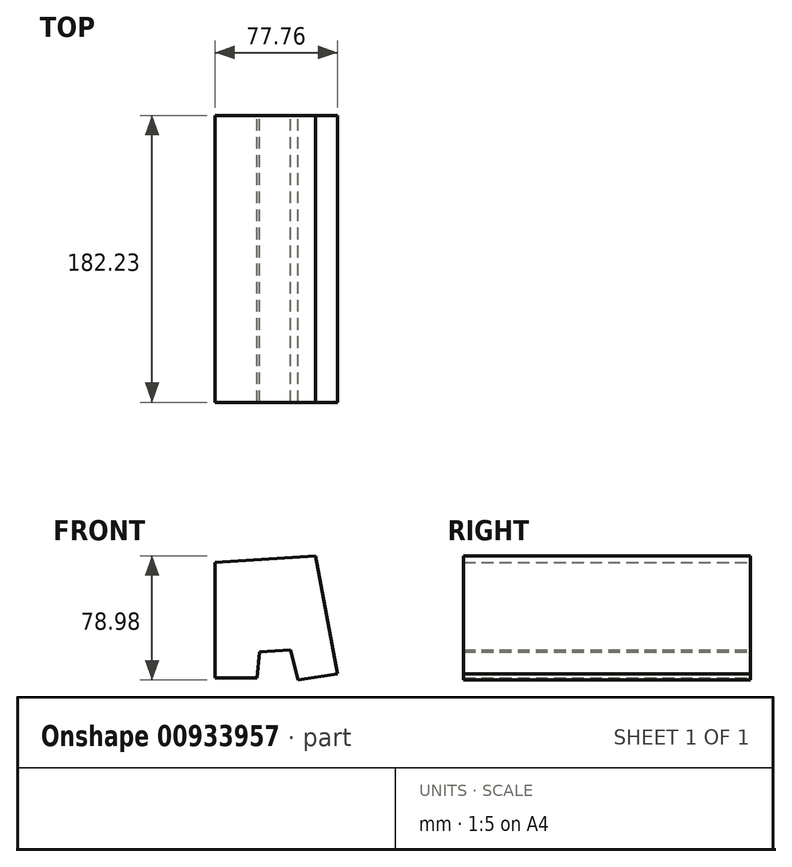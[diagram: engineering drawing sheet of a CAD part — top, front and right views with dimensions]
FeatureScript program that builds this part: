
annotation { "Feature Type Name" : "Feature", "Feature Type Description" : "" }
export const myFeature = defineFeature(function(context is Context, id is Id, definition is map)
    precondition{}
    {
        {
            var Q0;
            Q0=qCreatedBy(makeId("Front.planeOp"),FACE);
            var sketch = newSketch(context, id + "F0", { "sketchPlane" : qUnion([Q0])});
            skLineSegment(sketch, "E0", {"start": v(27.92, 44.57) * mm, "end": v(-35.76, 40.29) * mm});
            skLineSegment(sketch, "E1", {"start": v(-35.76, 40.29) * mm, "end": v(-35.76, -32.94) * mm});
            skLineSegment(sketch, "E2", {"start": v(-35.76, -32.94) * mm, "end": v(-9.06, -33.06) * mm});
            skLineSegment(sketch, "E3", {"start": v(-9.06, -33.06) * mm, "end": v(-7.6, -16.4) * mm});
            skLineSegment(sketch, "E4", {"start": v(-7.6, -16.4) * mm, "end": v(12.25, -15.3) * mm});
            skLineSegment(sketch, "E5", {"start": v(12.25, -15.3) * mm, "end": v(16.78, -34.41) * mm});
            skLineSegment(sketch, "E6", {"start": v(16.78, -34.41) * mm, "end": v(42, -30.5) * mm});
            skLineSegment(sketch, "E7", {"start": v(27.92, 44.57) * mm, "end": v(42, -30.5) * mm});
            skSolve(sketch);
        }
        {
            var Q0;
            Q0=makeQuery(id+"F0.imprint","IMPRINT",FACE,{"disambiguationData":[TD([[makeQuery(id+"F0.imprint","IMPRINT",EDGE,{"derivedFrom":sQuery(id+"F0.wireOp",EDGE,"E0")}),1.0]])]});
            extrude(context, id + "F1", {"entities" : qUnion([Q0]), "depth" : 182.23 * mm, "offsetDistance" : 25.4 * mm});
        }
    });
